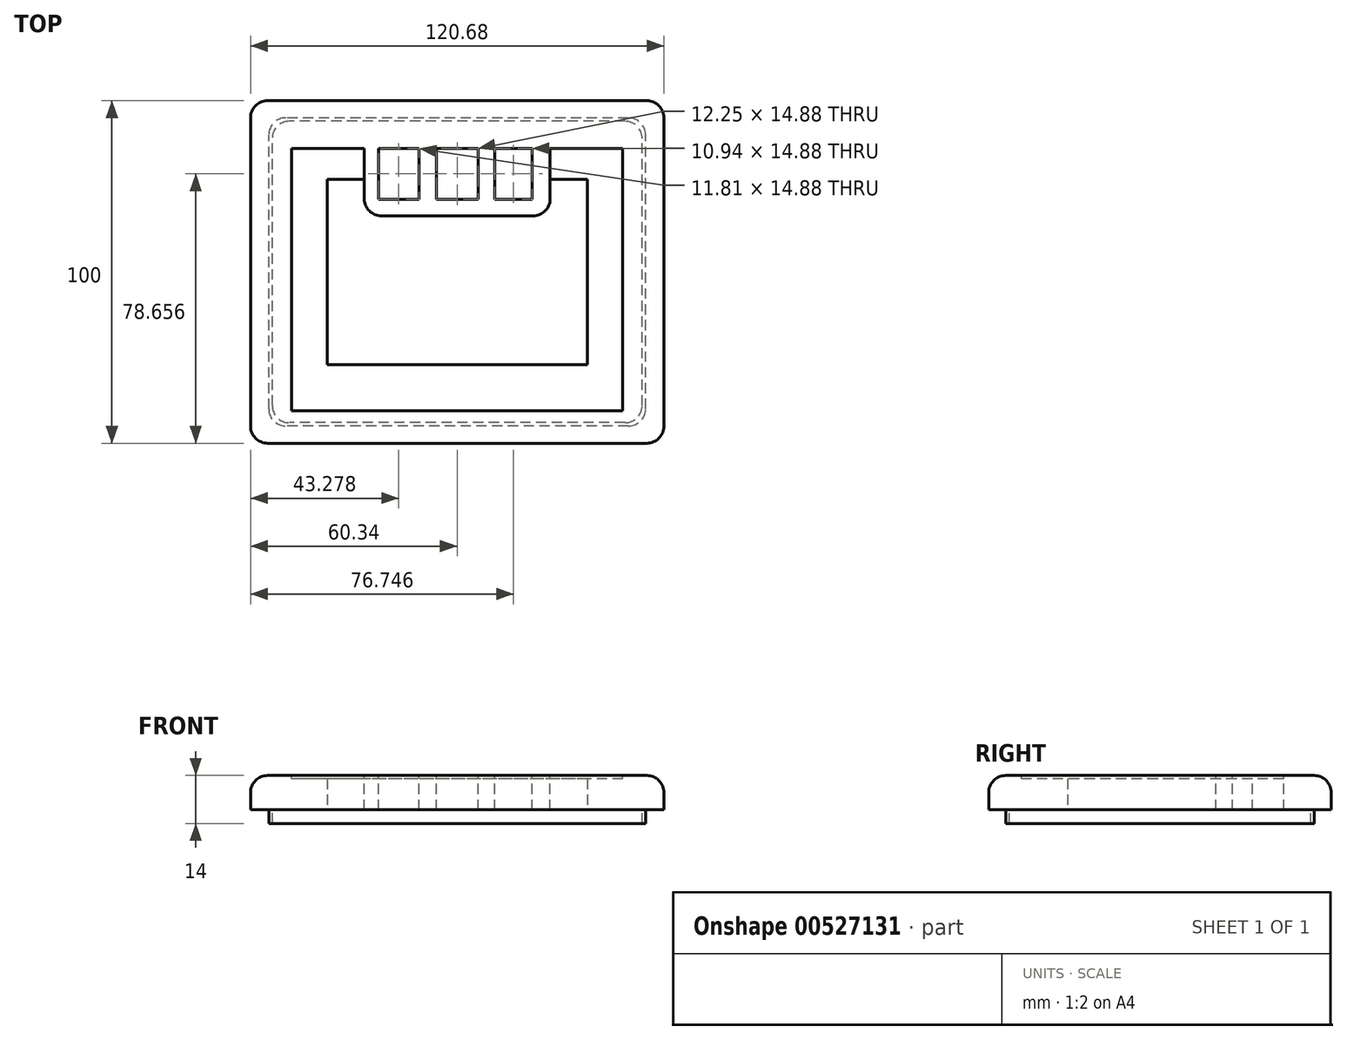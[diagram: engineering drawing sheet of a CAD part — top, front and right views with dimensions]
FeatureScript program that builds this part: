
annotation { "Feature Type Name" : "Feature", "Feature Type Description" : "" }
export const myFeature = defineFeature(function(context is Context, id is Id, definition is map)
    precondition{}
    {
        {
            var Q0;
            Q0=qCreatedBy(makeId("Top.planeOp"),FACE);
            var sketch = newSketch(context, id + "F0", { "sketchPlane" : qUnion([Q0])});
            skLineSegment(sketch, "E0.bottom", {"start": v(60.34, 50) * mm, "end": v(-60.34, 50) * mm});
            skLineSegment(sketch, "E0.top", {"start": v(60.34, -50) * mm, "end": v(-60.34, -50) * mm});
            skLineSegment(sketch, "E0.left", {"start": v(60.34, 50) * mm, "end": v(60.34, -50) * mm});
            skLineSegment(sketch, "E0.right", {"start": v(-60.34, 50) * mm, "end": v(-60.34, -50) * mm});
            skPoint(sketch, "E0.middle", {"position": v(0, 0) * mm});
            skPoint(sketch, "E1.visualSharp", {"position": v(-47, 44) * mm});
            skPoint(sketch, "E2.visualSharp", {"position": v(47, 44) * mm});
            skPoint(sketch, "E3.visualSharp", {"position": v(47, -44) * mm});
            skPoint(sketch, "E4.visualSharp", {"position": v(-47, -44) * mm});
            skLineSegment(sketch, "E5.bottom", {"start": v(38, 27) * mm, "end": v(-38, 27) * mm});
            skLineSegment(sketch, "E5.top", {"start": v(38, -27) * mm, "end": v(-38, -27) * mm});
            skLineSegment(sketch, "E5.left", {"start": v(38, 27) * mm, "end": v(38, -27) * mm});
            skLineSegment(sketch, "E5.right", {"start": v(-38, 27) * mm, "end": v(-38, -27) * mm});
            skSolve(sketch);
        }
        {
            var Q0;
            Q0=makeQuery(id+"F0.imprint","IMPRINT",FACE,{"disambiguationData":[TD([[makeQuery(id+"F0.imprint","IMPRINT",EDGE,{"derivedFrom":sQuery(id+"F0.wireOp",EDGE,"E0.bottom")}),1.0]])]});
            var Q1;
            Q1=makeQuery(id+"F0.imprint","IMPRINT",FACE,{"disambiguationData":[TD([[makeQuery(id+"F0.imprint","IMPRINT",EDGE,{"derivedFrom":sQuery(id+"F0.wireOp",EDGE,"Kfqqju8v-t6Ju-4E68-JE1m-NVa8dytUJgz5.bottom")}),1.0]])]});
            extrude(context, id + "F1", {"entities" : qUnion([Q0, Q1]), "depth" : 10 * mm, "offsetDistance" : 25 * mm});
        }
        {
            var Q0;
            Q0=makeQuery(id+"F1.opExtrude","CAP_FACE",FACE,{"disambiguationData":[OSD([sQuery(id+"F0.wireOp",EDGE,"E0.bottom"),sQuery(id+"F0.wireOp",EDGE,"E0.top"),sQuery(id+"F0.wireOp",EDGE,"E0.left"),sQuery(id+"F0.wireOp",EDGE,"E0.right"),sQuery(id+"F0.wireOp",EDGE,"Kfqqju8v-t6Ju-4E68-JE1m-NVa8dytUJgz5.top"),sQuery(id+"F0.wireOp",EDGE,"Kfqqju8v-t6Ju-4E68-JE1m-NVa8dytUJgz5.left"),sQuery(id+"F0.wireOp",EDGE,"Kfqqju8v-t6Ju-4E68-JE1m-NVa8dytUJgz5.right"),sQuery(id+"F0.wireOp",EDGE,"E1.filletArc"),sQuery(id+"F0.wireOp",EDGE,"E2.filletArc"),sQuery(id+"F0.wireOp",EDGE,"E3.filletArc"),sQuery(id+"F0.wireOp",EDGE,"E4.filletArc"),sQuery(id+"F0.wireOp",EDGE,"P3trXSsO-VMis-EaJn-KSxu-FRwLG4cPHZ6e"),sQuery(id+"F0.wireOp",EDGE,"qmgQdTMK-OTp5-ygfq-7OzS-3EU02hKRO2Nt"),sQuery(id+"F0.wireOp",EDGE,"XEvWEIhM-brhP-JIRv-dxkK-OmqC8tI9QrJq"),sQuery(id+"F0.wireOp",EDGE,"qNBkX408-eKR3-KtV5-qX16-dB4zIxC7iLcT"),sQuery(id+"F0.wireOp",EDGE,"rtT9LXhL-ydhv-9gyZ-7vST-5piBK125BLja")])],"isStart":true});
            var sketch = newSketch(context, id + "F2", { "sketchPlane" : qUnion([Q0])});
            skLineSegment(sketch, "E6.bottom", {"start": v(50, 45) * mm, "end": v(-50, 45) * mm});
            skLineSegment(sketch, "E6.top", {"start": v(50, -45) * mm, "end": v(-50, -45) * mm});
            skLineSegment(sketch, "E6.left", {"start": v(55, 40) * mm, "end": v(55, -40) * mm});
            skLineSegment(sketch, "E6.right", {"start": v(-55, 40) * mm, "end": v(-55, -40) * mm});
            skPoint(sketch, "E6.middle", {"position": v(0, 0) * mm});
            skLineSegment(sketch, "E7.bottom", {"start": v(49, 44) * mm, "end": v(-49, 44) * mm});
            skLineSegment(sketch, "E7.top", {"start": v(49, -44) * mm, "end": v(-49, -44) * mm});
            skLineSegment(sketch, "E7.left", {"start": v(54, 39) * mm, "end": v(54, -39) * mm});
            skLineSegment(sketch, "E7.right", {"start": v(-54, 39) * mm, "end": v(-54, -39) * mm});
            skPoint(sketch, "E8.visualSharp", {"position": v(-55, -45) * mm});
            skArc(sketch, "E8.filletArc", {"start": v(-55, -40) * mm, "mid": v(-53.54, -43.54) * mm, "end": v(-50, -45) * mm});
            skPoint(sketch, "E9.visualSharp", {"position": v(-54, -44) * mm});
            skArc(sketch, "E9.filletArc", {"start": v(-54, -39) * mm, "mid": v(-52.54, -42.54) * mm, "end": v(-49, -44) * mm});
            skPoint(sketch, "E10.visualSharp", {"position": v(-54, 44) * mm});
            skArc(sketch, "E10.filletArc", {"start": v(-49, 44) * mm, "mid": v(-52.54, 42.54) * mm, "end": v(-54, 39) * mm});
            skPoint(sketch, "E11.visualSharp", {"position": v(-55, 45) * mm});
            skArc(sketch, "E11.filletArc", {"start": v(-50, 45) * mm, "mid": v(-53.54, 43.54) * mm, "end": v(-55, 40) * mm});
            skPoint(sketch, "E12.visualSharp", {"position": v(54, 44) * mm});
            skArc(sketch, "E12.filletArc", {"start": v(54, 39) * mm, "mid": v(52.54, 42.54) * mm, "end": v(49, 44) * mm});
            skPoint(sketch, "E13.visualSharp", {"position": v(55, 45) * mm});
            skArc(sketch, "E13.filletArc", {"start": v(55, 40) * mm, "mid": v(53.54, 43.54) * mm, "end": v(50, 45) * mm});
            skPoint(sketch, "E14.visualSharp", {"position": v(54, -44) * mm});
            skArc(sketch, "E14.filletArc", {"start": v(49, -44) * mm, "mid": v(52.54, -42.54) * mm, "end": v(54, -39) * mm});
            skPoint(sketch, "E15.visualSharp", {"position": v(55, -45) * mm});
            skArc(sketch, "E15.filletArc", {"start": v(50, -45) * mm, "mid": v(53.54, -43.54) * mm, "end": v(55, -40) * mm});
            skSolve(sketch);
        }
        {
            var Q0;
            Q0=makeQuery(id+"F2.imprint","IMPRINT",FACE,{"disambiguationData":[TD([[makeQuery(id+"F2.imprint","IMPRINT",EDGE,{"derivedFrom":sQuery(id+"F2.wireOp",EDGE,"E6.bottom")}),1.0]])]});
            extrude(context, id + "F3", {"entities" : qUnion([Q0]), "operationType" : NewBodyOperationType.ADD, "depth" : 4 * mm, "offsetDistance" : 25 * mm});
        }
        {
            var Q0;
            Q0=makeQuery(id+"F1.opExtrude","SWEPT_EDGE",EDGE,{"disambiguationData":[OSD([sQuery(id+"F0.wireOp",EDGE,"E0.top"),sQuery(id+"F0.wireOp",EDGE,"E0.right")])]});
            var Q1;
            Q1=makeQuery(id+"F1.opExtrude","SWEPT_EDGE",EDGE,{"disambiguationData":[OSD([sQuery(id+"F0.wireOp",EDGE,"E0.top"),sQuery(id+"F0.wireOp",EDGE,"E0.left")])]});
            var Q2;
            Q2=makeQuery(id+"F1.opExtrude","SWEPT_EDGE",EDGE,{"disambiguationData":[OSD([sQuery(id+"F0.wireOp",EDGE,"E0.bottom"),sQuery(id+"F0.wireOp",EDGE,"E0.left")])]});
            var Q3;
            Q3=makeQuery(id+"F1.opExtrude","SWEPT_EDGE",EDGE,{"disambiguationData":[OSD([sQuery(id+"F0.wireOp",EDGE,"E0.bottom"),sQuery(id+"F0.wireOp",EDGE,"E0.right")])]});
            var Q4;
            Q4=makeQuery(id+"F1.opExtrude","CAP_EDGE",EDGE,{"disambiguationData":[OSD([sQuery(id+"F0.wireOp",EDGE,"E0.bottom")])],"isStart":false});
            var Q5;
            Q5=makeQuery(id+"F1.opExtrude","CAP_EDGE",EDGE,{"disambiguationData":[OSD([sQuery(id+"F0.wireOp",EDGE,"E0.right")])],"isStart":false});
            var Q6;
            Q6=makeQuery(id+"F1.opExtrude","CAP_EDGE",EDGE,{"disambiguationData":[OSD([sQuery(id+"F0.wireOp",EDGE,"E0.top")])],"isStart":false});
            var Q7;
            Q7=makeQuery(id+"F1.opExtrude","CAP_EDGE",EDGE,{"disambiguationData":[OSD([sQuery(id+"F0.wireOp",EDGE,"E0.left")])],"isStart":false});
            fillet(context, id + "F4", {"entities" : qUnion([Q0, Q1, Q2, Q3, Q4, Q5, Q6, Q7]), "radius" : 5 * mm, "tangentPropagation" : true, "allowEdgeOverflow" : false});
        }
        {
            var Q0;
            Q0=makeQuery(id+"F1.opExtrude","CAP_FACE",FACE,{"disambiguationData":[OSD([sQuery(id+"F0.wireOp",EDGE,"E0.bottom"),sQuery(id+"F0.wireOp",EDGE,"E0.top"),sQuery(id+"F0.wireOp",EDGE,"E0.left"),sQuery(id+"F0.wireOp",EDGE,"E0.right"),sQuery(id+"F0.wireOp",EDGE,"E5.bottom"),sQuery(id+"F0.wireOp",EDGE,"E5.top"),sQuery(id+"F0.wireOp",EDGE,"E5.left"),sQuery(id+"F0.wireOp",EDGE,"E5.right")])],"isStart":false});
            var sketch = newSketch(context, id + "F5", { "sketchPlane" : qUnion([Q0])});
            skLineSegment(sketch, "E16.bottom", {"start": v(48.78, 37.62) * mm, "end": v(-48.78, 37.62) * mm});
            skLineSegment(sketch, "E16.top", {"start": v(48.78, -37.62) * mm, "end": v(-48.78, -37.62) * mm});
            skLineSegment(sketch, "E16.left", {"start": v(48.78, 37.62) * mm, "end": v(48.78, -37.62) * mm});
            skLineSegment(sketch, "E16.right", {"start": v(-48.78, 37.62) * mm, "end": v(-48.78, -37.62) * mm});
            skPoint(sketch, "E16.middle", {"position": v(0, 0) * mm});
            skLineSegment(sketch, "E17.bottom", {"start": v(27.13, 37.62) * mm, "end": v(-27.13, 37.62) * mm});
            skLineSegment(sketch, "E17.top", {"start": v(27.13, 16.38) * mm, "end": v(-27.13, 16.38) * mm});
            skLineSegment(sketch, "E17.left", {"start": v(27.13, 37.62) * mm, "end": v(27.13, 16.38) * mm});
            skLineSegment(sketch, "E17.right", {"start": v(-27.13, 37.62) * mm, "end": v(-27.13, 16.38) * mm});
            skPoint(sketch, "E17.middle", {"position": v(0, 27) * mm});
            skSolve(sketch);
        }
        {
            var Q0;
            {var subQ0=sQuery(id+"F5.wireOp",EDGE,"E17.top");Q0=makeQuery(id+"F5.imprint","IMPRINT",FACE,{"disambiguationData":[TD([[makeQuery(id+"F5.imprint","IMPRINT",EDGE,{"derivedFrom":subQ0}),-1.0]])]});}
            extrude(context, id + "F6", {"entities" : qUnion([Q0]), "operationType" : NewBodyOperationType.ADD, "oppositeDirection" : true, "depth" : 10 * mm, "offsetDistance" : 25 * mm});
        }
        {
            var Q0;
            {var subQ0=sQuery(id+"F0.wireOp",EDGE,"E5.bottom");Q0=makeQuery(id+"F6.boolean.opBoolean","MERGE",FACE,{"derivedFrom":[makeQuery(id+"F1.opExtrude","CAP_FACE",FACE,{"disambiguationData":[OSD([sQuery(id+"F0.wireOp",EDGE,"E0.bottom"),sQuery(id+"F0.wireOp",EDGE,"E0.top"),sQuery(id+"F0.wireOp",EDGE,"E0.left"),sQuery(id+"F0.wireOp",EDGE,"E0.right"),subQ0,sQuery(id+"F0.wireOp",EDGE,"E5.top"),sQuery(id+"F0.wireOp",EDGE,"E5.left"),sQuery(id+"F0.wireOp",EDGE,"E5.right")])],"isStart":false}),makeQuery(id+"F6.opExtrude","CAP_FACE",FACE,{"disambiguationData":[OSD([subQ0,sQuery(id+"F5.wireOp",EDGE,"E17.top"),sQuery(id+"F5.wireOp",EDGE,"E17.left"),sQuery(id+"F5.wireOp",EDGE,"E17.right")])],"isStart":true})]});}
            var sketch = newSketch(context, id + "F7", { "sketchPlane" : qUnion([Q0])});
            skLineSegment(sketch, "E18.bottom", {"start": v(48.34, 36.1) * mm, "end": v(-48.34, 36.1) * mm});
            skLineSegment(sketch, "E18.top", {"start": v(48.34, -40.47) * mm, "end": v(-48.34, -40.47) * mm});
            skLineSegment(sketch, "E18.left", {"start": v(48.34, 36.1) * mm, "end": v(48.34, -40.47) * mm});
            skLineSegment(sketch, "E18.right", {"start": v(-48.34, 36.1) * mm, "end": v(-48.34, -40.47) * mm});
            skPoint(sketch, "E18.middle", {"position": v(0, -2.19) * mm});
            skLineSegment(sketch, "E19.bottom", {"start": v(27.13, 36.1) * mm, "end": v(-27.13, 36.1) * mm});
            skLineSegment(sketch, "E19.top", {"start": v(27.13, 17.9) * mm, "end": v(-27.13, 17.9) * mm});
            skLineSegment(sketch, "E19.left", {"start": v(27.13, 36.1) * mm, "end": v(27.13, 17.9) * mm});
            skLineSegment(sketch, "E19.right", {"start": v(-27.13, 36.1) * mm, "end": v(-27.13, 17.9) * mm});
            skPoint(sketch, "E19.middle", {"position": v(0, 27) * mm});
            skPoint(sketch, "E19.middle.positionSnap0", {"position": v(0, 16.38) * mm});
            skPoint(sketch, "E19.centerSnap0", {"position": v(0, 16.38) * mm});
            skSolve(sketch);
        }
        {
            var Q0;
            Q0=makeQuery(id+"F7.imprint","IMPRINT",FACE,{"disambiguationData":[TD([[makeQuery(id+"F7.imprint","IMPRINT",EDGE,{"derivedFrom":sQuery(id+"F7.wireOp",EDGE,"E18.top")}),-1.0]])]});
            extrude(context, id + "F8", {"entities" : qUnion([Q0]), "operationType" : NewBodyOperationType.REMOVE, "oppositeDirection" : true, "depth" : 1 * mm, "offsetDistance" : 25 * mm});
        }
        {
            var Q0;
            {var subQ0=sQuery(id+"F0.wireOp",EDGE,"E5.bottom");Q0=makeQuery(id+"F6.boolean.opBoolean","MERGE",FACE,{"derivedFrom":[makeQuery(id+"F1.opExtrude","CAP_FACE",FACE,{"disambiguationData":[OSD([sQuery(id+"F0.wireOp",EDGE,"E0.bottom"),sQuery(id+"F0.wireOp",EDGE,"E0.top"),sQuery(id+"F0.wireOp",EDGE,"E0.left"),sQuery(id+"F0.wireOp",EDGE,"E0.right"),subQ0,sQuery(id+"F0.wireOp",EDGE,"E5.top"),sQuery(id+"F0.wireOp",EDGE,"E5.left"),sQuery(id+"F0.wireOp",EDGE,"E5.right")])],"isStart":false}),makeQuery(id+"F6.opExtrude","CAP_FACE",FACE,{"disambiguationData":[OSD([subQ0,sQuery(id+"F5.wireOp",EDGE,"E17.top"),sQuery(id+"F5.wireOp",EDGE,"E17.left"),sQuery(id+"F5.wireOp",EDGE,"E17.right")])],"isStart":true})]});}
            var sketch = newSketch(context, id + "F9", { "sketchPlane" : qUnion([Q0])});
            skLineSegment(sketch, "E20.bottom", {"start": v(6.13, 36.1) * mm, "end": v(-6.13, 36.1) * mm});
            skLineSegment(sketch, "E20.top", {"start": v(6.13, 21.22) * mm, "end": v(-6.13, 21.22) * mm});
            skLineSegment(sketch, "E20.left", {"start": v(6.13, 36.1) * mm, "end": v(6.13, 21.22) * mm});
            skLineSegment(sketch, "E20.right", {"start": v(-6.13, 36.1) * mm, "end": v(-6.13, 21.22) * mm});
            skPoint(sketch, "E20.middle", {"position": v(0, 28.66) * mm});
            skLineSegment(sketch, "E21.bottom", {"start": v(21.87, 36.1) * mm, "end": v(10.94, 36.1) * mm});
            skLineSegment(sketch, "E21.top", {"start": v(21.87, 21.22) * mm, "end": v(10.94, 21.22) * mm});
            skLineSegment(sketch, "E21.left", {"start": v(21.87, 36.1) * mm, "end": v(21.87, 21.22) * mm});
            skLineSegment(sketch, "E21.right", {"start": v(10.94, 36.1) * mm, "end": v(10.94, 21.22) * mm});
            skPoint(sketch, "E21.middle", {"position": v(16.4, 28.66) * mm});
            skLineSegment(sketch, "E22.bottom", {"start": v(-11.16, 36.1) * mm, "end": v(-22.97, 36.1) * mm});
            skLineSegment(sketch, "E22.top", {"start": v(-11.16, 21.22) * mm, "end": v(-22.97, 21.22) * mm});
            skLineSegment(sketch, "E22.left", {"start": v(-11.16, 36.1) * mm, "end": v(-11.16, 21.22) * mm});
            skLineSegment(sketch, "E22.right", {"start": v(-22.97, 36.1) * mm, "end": v(-22.97, 21.22) * mm});
            skPoint(sketch, "E22.middle", {"position": v(-17.06, 28.66) * mm});
            skSolve(sketch);
        }
        {
            var Q0;
            Q0=makeQuery(id+"F9.imprint","IMPRINT",FACE,{"disambiguationData":[TD([[makeQuery(id+"F9.imprint","IMPRINT",EDGE,{"derivedFrom":sQuery(id+"F9.wireOp",EDGE,"E22.bottom")}),1.0]])]});
            var Q1;
            Q1=makeQuery(id+"F9.imprint","IMPRINT",FACE,{"disambiguationData":[TD([[makeQuery(id+"F9.imprint","IMPRINT",EDGE,{"derivedFrom":sQuery(id+"F9.wireOp",EDGE,"E20.bottom")}),1.0]])]});
            var Q2;
            Q2=makeQuery(id+"F9.imprint","IMPRINT",FACE,{"disambiguationData":[TD([[makeQuery(id+"F9.imprint","IMPRINT",EDGE,{"derivedFrom":sQuery(id+"F9.wireOp",EDGE,"E21.bottom")}),1.0]])]});
            extrude(context, id + "F10", {"entities" : qUnion([Q0, Q1, Q2]), "operationType" : NewBodyOperationType.REMOVE, "oppositeDirection" : true, "depth" : 25 * mm, "offsetDistance" : 25 * mm});
        }
        {
            var Q0;
            Q0=makeQuery(id+"F6.opExtrude","SWEPT_EDGE",EDGE,{"disambiguationData":[OSD([sQuery(id+"F5.wireOp",EDGE,"E17.top"),sQuery(id+"F5.wireOp",EDGE,"E17.right")])]});
            var Q1;
            Q1=makeQuery(id+"F6.opExtrude","SWEPT_EDGE",EDGE,{"disambiguationData":[OSD([sQuery(id+"F5.wireOp",EDGE,"E17.top"),sQuery(id+"F5.wireOp",EDGE,"E17.left")])]});
            fillet(context, id + "F11", {"entities" : qUnion([Q0, Q1]), "radius" : 5 * mm, "tangentPropagation" : true, "allowEdgeOverflow" : false});
        }
    });
